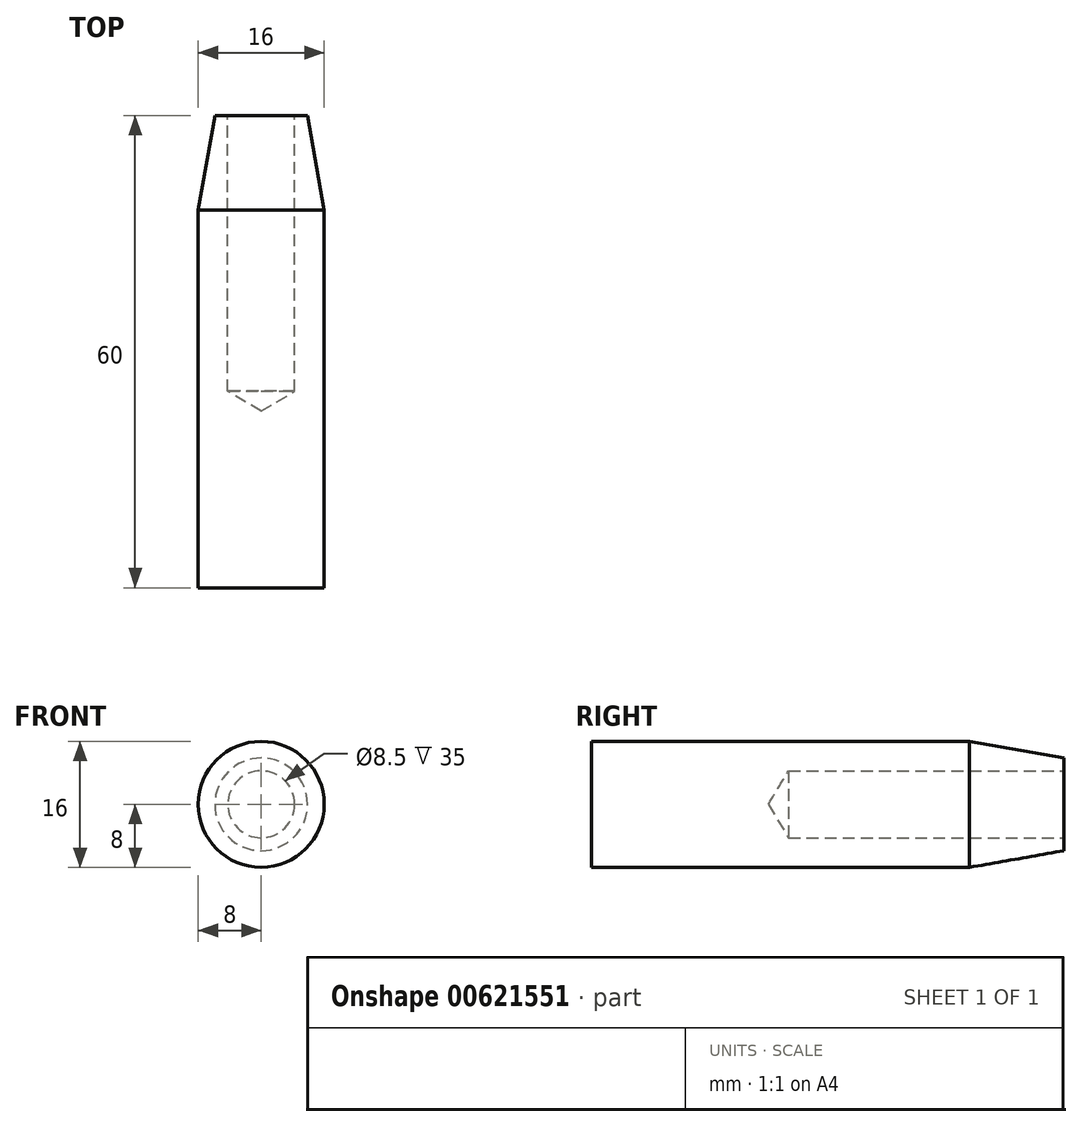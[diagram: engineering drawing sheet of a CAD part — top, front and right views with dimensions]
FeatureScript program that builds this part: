
annotation { "Feature Type Name" : "Feature", "Feature Type Description" : "" }
export const myFeature = defineFeature(function(context is Context, id is Id, definition is map)
    precondition{}
    {
        {
            var Q0;
            Q0=qCreatedBy(makeId("Front.planeOp"),FACE);
            var sketch = newSketch(context, id + "F0", { "sketchPlane" : qUnion([Q0])});
            skCircle(sketch, "E0", {"center": v(0, 0) * mm, "radius": 8 * mm});
            skSolve(sketch);
        }
        {
            var Q0;
            Q0 = qSketchRegion(id + "F0", true);
            extrude(context, id + "F1", {"entities" : qUnion([Q0]), "depth" : 60 * mm, "offsetDistance" : 25 * mm});
        }
        {
            var Q0;
            Q0=makeQuery(id+"F1.opExtrude","CAP_FACE",FACE,{"disambiguationData":[OSD([sQuery(id+"F0.wireOp",EDGE,"E0")])],"isStart":true});
            var sketch = newSketch(context, id + "F2", { "sketchPlane" : qUnion([Q0])});
            skPoint(sketch, "E1", {"position": v(0, 0) * mm});
            skSolve(sketch);
        }
        {
            var Q0;
            Q0=sQuery(id+"F2.wireOp",VERTEX,"E1");
            var Q1;
            Q1=makeQuery(id+"F1.opExtrude","SWEPT_BODY",BODY,{"disambiguationData":[OSD([sQuery(id+"F0.wireOp",EDGE,"E0")])]});
            hole(context, id + "F3", {"style" : HoleStyle.SIMPLE, "endStyle" : HoleEndStyle.BLIND, "standardTappedOrClearance" : lookupTablePath({ "standard" : "ISO", "engagement" : "75%", "pitch" : "1.5 mm", "size" : "M10", "type" : "Tapped" }), "standardBlindInLast" : lookupTablePath({ "standard" : "ISO", "engagement" : "75%", "pitch" : "1.5 mm", "size" : "M10", "type" : "Tapped" }), "holeDiameter" : 8.5 * mm, "majorDiameter" : 10 * mm, "showTappedDepth" : true, "holeDepth" : 35 * mm, "isTappedThrough" : true, "tappedDepth" : 30.5 * mm, "tapClearance" : 3, "startFromSketch" : true, "locations" : qUnion([Q0]), "scope" : qUnion([Q1])});
        }
        {
            var Q0;
            Q0=makeQuery(id+"F1.opExtrude","CAP_EDGE",EDGE,{"disambiguationData":[OSD([sQuery(id+"F0.wireOp",EDGE,"E0")])],"isStart":true});
            chamfer(context, id + "F4", {"entities" : qUnion([Q0]), "chamferType" : ChamferType.OFFSET_ANGLE, "width" : 12 * mm, "oppositeDirection" : false, "angle" : 10 * degree, "tangentPropagation" : true});
        }
    });
